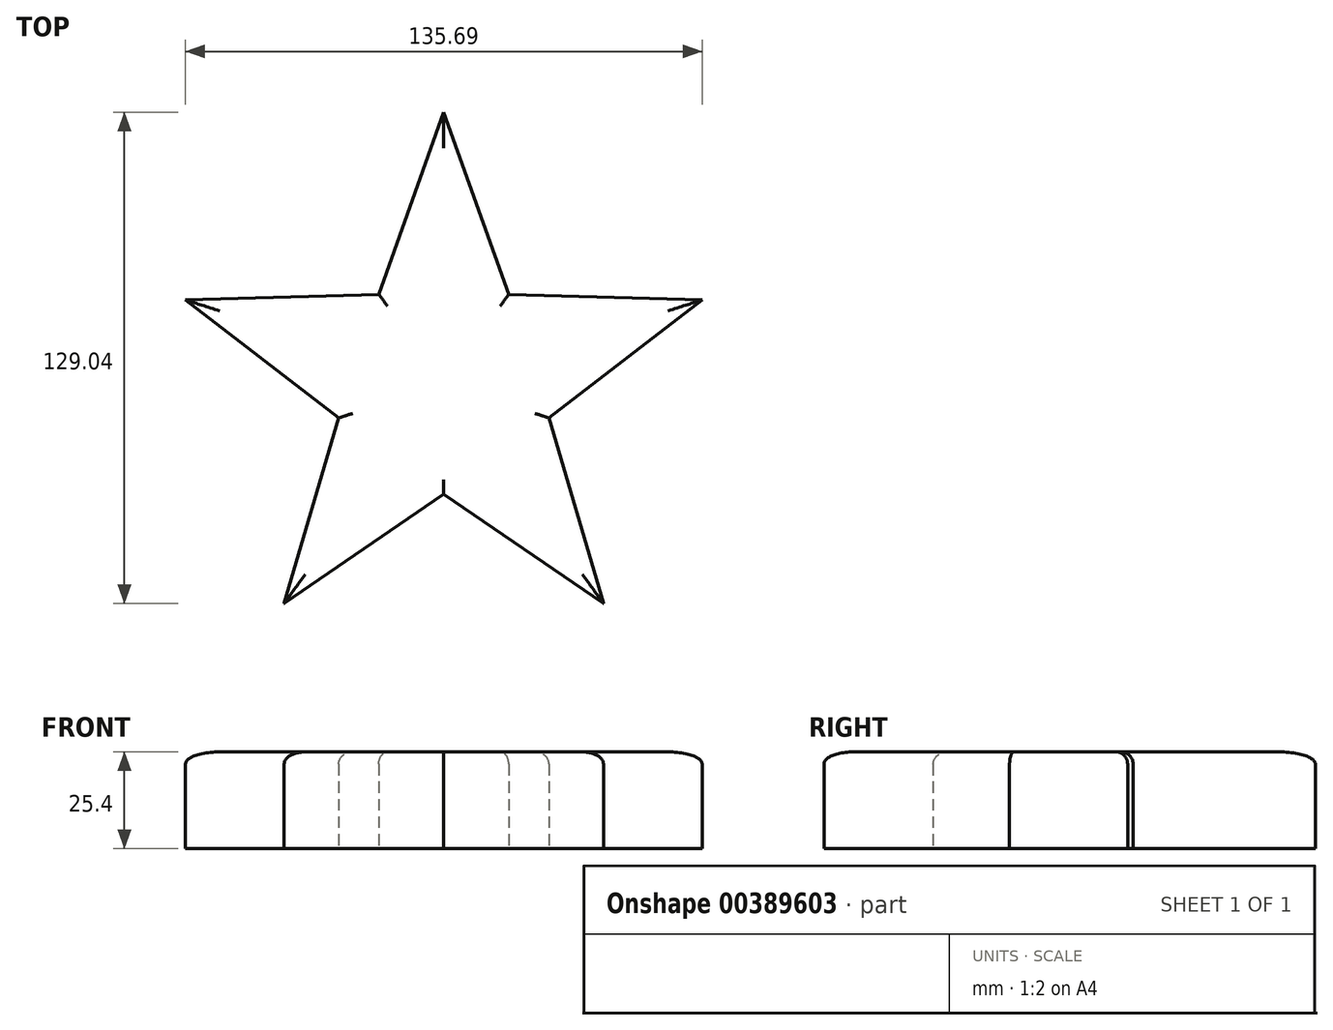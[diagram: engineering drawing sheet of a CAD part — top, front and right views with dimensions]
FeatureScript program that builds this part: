
annotation { "Feature Type Name" : "Feature", "Feature Type Description" : "" }
export const myFeature = defineFeature(function(context is Context, id is Id, definition is map)
    precondition{}
    {
        {
            var Q0;
            Q0=qCreatedBy(makeId("Top.planeOp"),FACE);
            var sketch = newSketch(context, id + "F0", { "sketchPlane" : qUnion([Q0])});
            skLineSegment(sketch, "E0.MirrorCS", {"start": v(16.67, 18.8) * mm, "end": v(-0.4, 66.65) * mm});
            skLineSegment(sketch, "E1.1.0", {"start": v(-28, -13.65) * mm, "end": v(-68.24, 17.36) * mm});
            skLineSegment(sketch, "E1.1.1", {"start": v(-17.46, 18.8) * mm, "end": v(-68.24, 17.36) * mm});
            skLineSegment(sketch, "E1.2.0", {"start": v(-0.4, -33.7) * mm, "end": v(-42.32, -62.39) * mm});
            skLineSegment(sketch, "E1.3.0", {"start": v(27.21, -13.65) * mm, "end": v(41.53, -62.39) * mm});
            skLineSegment(sketch, "E1.4.0", {"start": v(16.67, 18.8) * mm, "end": v(67.45, 17.36) * mm});
            skLineSegment(sketch, "E2.trimOffspring", {"start": v(-17.46, 18.8) * mm, "end": v(-0.4, 66.65) * mm});
            skLineSegment(sketch, "E3.trimOffspring", {"start": v(-28, -13.65) * mm, "end": v(-42.32, -62.39) * mm});
            skLineSegment(sketch, "E4.trimOffspring", {"start": v(27.21, -13.65) * mm, "end": v(67.45, 17.36) * mm});
            skLineSegment(sketch, "E5.trimOffspring", {"start": v(-0.4, -33.7) * mm, "end": v(41.53, -62.39) * mm});
            skPoint(sketch, "E6.center", {"position": v(0, 0.2) * mm});
            skSolve(sketch);
        }
        {
            var Q0;
            Q0=makeQuery(id+"F0.imprint","IMPRINT",FACE,{"disambiguationData":[TD([[makeQuery(id+"F0.imprint","IMPRINT",EDGE,{"derivedFrom":sQuery(id+"F0.wireOp",EDGE,"E0.MirrorCS")}),1.0]])]});
            extrude(context, id + "F1", {"entities" : qUnion([Q0]), "depth" : 25.4 * mm});
        }
        {
            var Q0;
            Q0=makeQuery(id+"F1.opExtrude","CAP_FACE",FACE,{"disambiguationData":[OSD([sQuery(id+"F0.wireOp",EDGE,"E0.MirrorCS"),sQuery(id+"F0.wireOp",EDGE,"E1.1.0"),sQuery(id+"F0.wireOp",EDGE,"E1.1.1"),sQuery(id+"F0.wireOp",EDGE,"E1.2.0"),sQuery(id+"F0.wireOp",EDGE,"E1.3.0"),sQuery(id+"F0.wireOp",EDGE,"E1.4.0"),sQuery(id+"F0.wireOp",EDGE,"E2.trimOffspring"),sQuery(id+"F0.wireOp",EDGE,"E3.trimOffspring"),sQuery(id+"F0.wireOp",EDGE,"E4.trimOffspring"),sQuery(id+"F0.wireOp",EDGE,"E5.trimOffspring")])],"isStart":false});
            fillet(context, id + "F2", {"entities" : qUnion([Q0]), "radius" : 3.17 * mm, "tangentPropagation" : true, "allowEdgeOverflow" : false});
        }
    });
